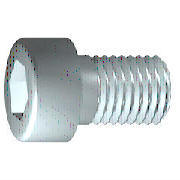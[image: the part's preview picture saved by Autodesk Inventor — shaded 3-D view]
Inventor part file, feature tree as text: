
AUTODESK INVENTOR PART (.ipt)
format: ipt  version: 2023.3 (Build 273359000, 359)  size: 196,608 bytes
history: native  units: mm (DEFAULTED — no unit token found)
features: sketch x2, other x1, extrude x1, plane x1, fillet x1
ambient origin geometry x7: Origin, YZ Plane, XY Plane, X Axis, Y Axis, Z Axis, Center Point
bodies: Solid1 (feature_tree)
feature tree (6):
  other  "Körper"
  extrude  "Loch"  Depth=3.0mm
  plane  "Work Plane1"
  fillet  "Fillet2"  Radius=3.0mm
  sketch  "Skizze1"  dims[d1=3.75mm d2=0.306825mm d3=3.0mm]
  sketch  "Skizze2"  dims[d4=1.3mm d5=60.0deg d6=3.0mm d7=3.0mm d8=2.886751mm d9=5.5mm d10=90.0deg d11=10.0mm d12=0.0mm d13=3.75mm d14=0.0mm d15=0.306725mm d16=0.306725mm d17=0.3mm d19=0.0mm d26=5.0mm d27=45.0deg d28=0.0mm d29=0.0mm d30=0.1mm]
